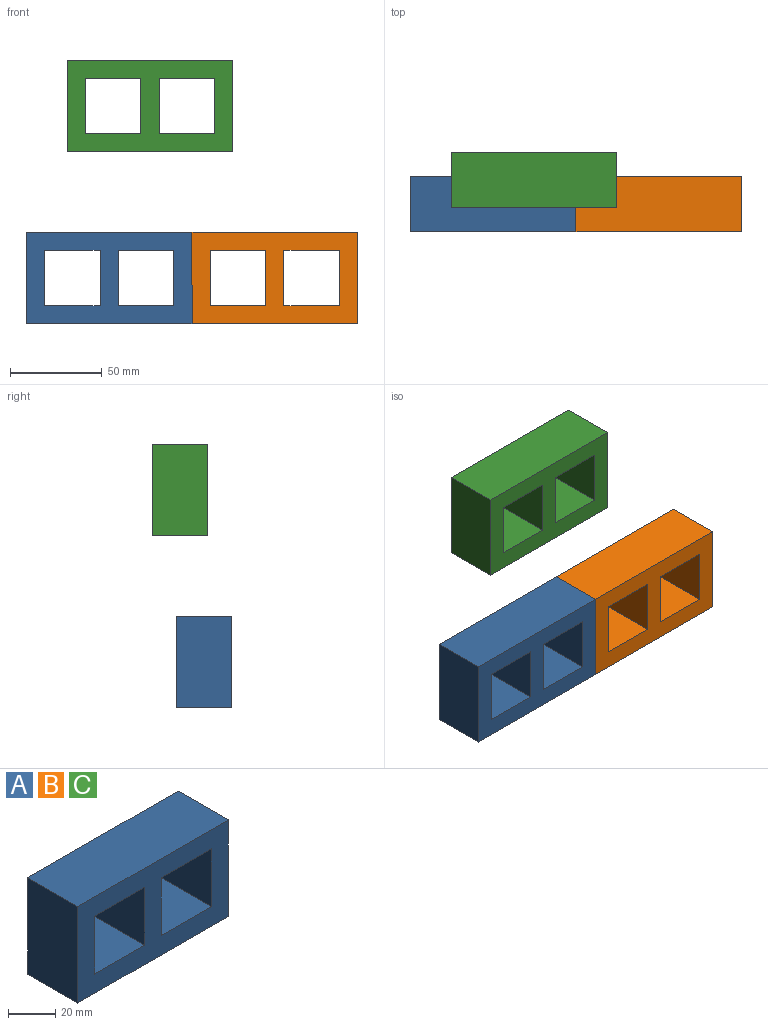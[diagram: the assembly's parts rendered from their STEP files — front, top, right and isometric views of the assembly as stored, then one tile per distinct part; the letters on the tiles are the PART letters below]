
ASSEMBLY  parts=3 mates=1
PART A: 14 faces, bbox 90x30x50 mm
  f0: plane 90x30mm, normal (0,0,1), area 2700mm2, adj f1,f3,f4,f5
  f1: plane 50x30mm, normal (-1,0,0), area 1500mm2, adj f0,f2,f4,f5
  f2: plane 90x30mm, normal (0,0,-1), area 2700mm2, adj f1,f3,f4,f5
  f3: plane 50x30mm, normal (1,0,0), area 1500mm2, adj f0,f2,f4,f5
  f4: plane 90x50mm, normal (0,-1,0), area 2700mm2, adj f0,f1,f2,f3,f6,f7,f8,f9
  f5: plane 90x50mm, normal (0,1,0), area 2700mm2, adj f0,f1,f2,f3,f6,f7,f8,f9
  f6: plane 30x30mm, normal (0,0,-1), area 900mm2, adj f4,f5,f7,f9
  f7: plane 30x30mm, normal (1,0,0), area 900mm2, adj f4,f5,f6,f8
  f8: plane 30x30mm, normal (0,0,1), area 900mm2, adj f4,f5,f7,f9
  f9: plane 30x30mm, normal (-1,0,0), area 900mm2, adj f4,f5,f6,f8
  f10: plane 30x30mm, normal (0,0,-1), area 900mm2, adj f4,f5,f11,f13
  f11: plane 30x30mm, normal (1,0,0), area 900mm2, adj f4,f5,f10,f12
  f12: plane 30x30mm, normal (0,0,1), area 900mm2, adj f4,f5,f11,f13
  f13: plane 30x30mm, normal (-1,0,0), area 900mm2, adj f4,f5,f10,f12
PART B: same geometry as A
PART C: same geometry as A
PLACE A t=(-96.16,22.58,-10.78)mm
PLACE B t=(-6.16,22.58,-10.78)mm
PLACE C t=(-73.99,35.51,82.71)mm
MATE fastened A.f3 <-> B.f1  axis (1,0,0) through (-29.82,7.58,-10.6)mm
